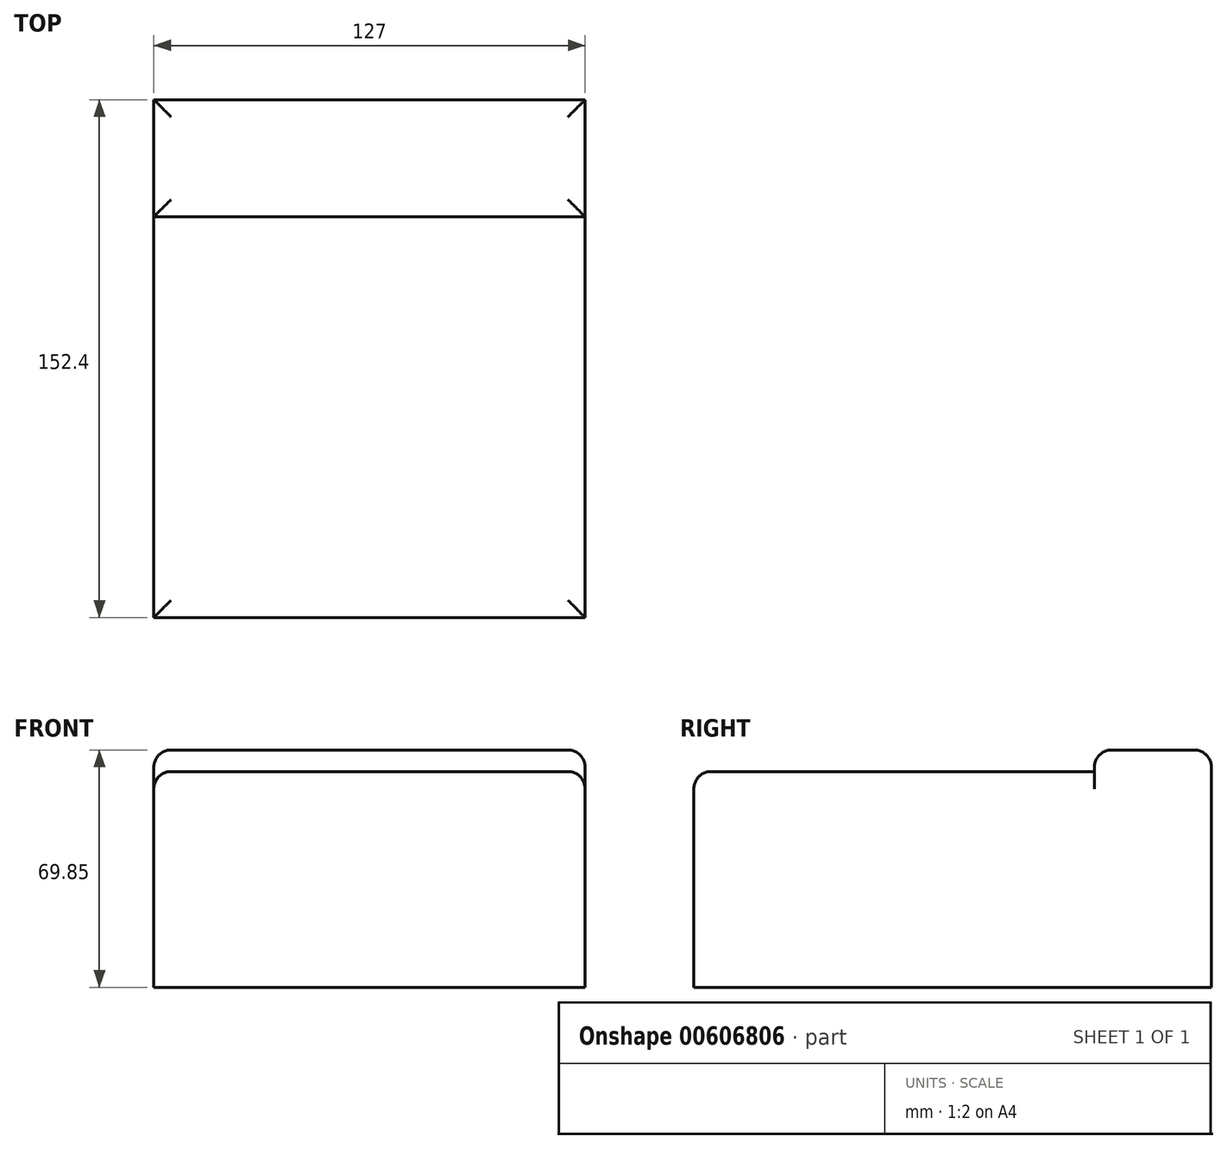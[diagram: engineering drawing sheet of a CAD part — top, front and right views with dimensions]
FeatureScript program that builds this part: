
annotation { "Feature Type Name" : "Feature", "Feature Type Description" : "" }
export const myFeature = defineFeature(function(context is Context, id is Id, definition is map)
    precondition{}
    {
        {
            var Q0;
            Q0=qCreatedBy(makeId("Top.planeOp"),FACE);
            var sketch = newSketch(context, id + "F0", { "sketchPlane" : qUnion([Q0])});
            skLineSegment(sketch, "E0.bottom", {"start": v(-73.34, 101.78) * mm, "end": v(53.66, 101.78) * mm});
            skLineSegment(sketch, "E0.top", {"start": v(-73.34, -50.62) * mm, "end": v(53.66, -50.62) * mm});
            skLineSegment(sketch, "E0.left", {"start": v(-73.34, 101.78) * mm, "end": v(-73.34, -50.62) * mm});
            skLineSegment(sketch, "E0.right", {"start": v(53.66, 101.78) * mm, "end": v(53.66, -50.62) * mm});
            skSolve(sketch);
        }
        {
            var Q0;
            Q0 = qSketchRegion(id + "F0", true);
            extrude(context, id + "F1", {"entities" : qUnion([Q0]), "depth" : 63.5 * mm, "offsetDistance" : 25.4 * mm});
        }
        {
            var Q0;
            Q0=makeQuery(id+"F1.opExtrude","CAP_FACE",FACE,{"disambiguationData":[OSD([sQuery(id+"F0.wireOp",EDGE,"E0.bottom"),sQuery(id+"F0.wireOp",EDGE,"E0.top"),sQuery(id+"F0.wireOp",EDGE,"E0.left"),sQuery(id+"F0.wireOp",EDGE,"E0.right")])],"isStart":false});
            var sketch = newSketch(context, id + "F2", { "sketchPlane" : qUnion([Q0])});
            skLineSegment(sketch, "E1.bottom", {"start": v(-73.34, 101.78) * mm, "end": v(53.66, 101.78) * mm});
            skLineSegment(sketch, "E1.top", {"start": v(-73.34, 67.31) * mm, "end": v(53.66, 67.31) * mm});
            skLineSegment(sketch, "E1.left", {"start": v(-73.34, 101.78) * mm, "end": v(-73.34, 67.31) * mm});
            skLineSegment(sketch, "E1.right", {"start": v(53.66, 101.78) * mm, "end": v(53.66, 67.31) * mm});
            skSolve(sketch);
        }
        {
            var Q0;
            Q0 = qSketchRegion(id + "F2", true);
            extrude(context, id + "F3", {"entities" : qUnion([Q0]), "operationType" : NewBodyOperationType.ADD, "depth" : 6.35 * mm, "offsetDistance" : 25.4 * mm});
        }
        {
            var Q0;
            Q0=makeQuery(id+"F3.opExtrude","CAP_EDGE",EDGE,{"disambiguationData":[OSD([sQuery(id+"F2.wireOp",EDGE,"E1.top")])],"isStart":false});
            var Q1;
            Q1=makeQuery(id+"F1.opExtrude","CAP_EDGE",EDGE,{"disambiguationData":[OSD([sQuery(id+"F0.wireOp",EDGE,"E0.right")])],"isStart":false});
            var Q2;
            Q2=makeQuery(id+"F1.opExtrude","CAP_EDGE",EDGE,{"disambiguationData":[OSD([sQuery(id+"F0.wireOp",EDGE,"E0.top")])],"isStart":false});
            var Q3;
            Q3=makeQuery(id+"F1.opExtrude","CAP_EDGE",EDGE,{"disambiguationData":[OSD([sQuery(id+"F0.wireOp",EDGE,"E0.left")])],"isStart":false});
            var Q4;
            Q4=makeQuery(id+"F3.opExtrude","CAP_EDGE",EDGE,{"disambiguationData":[OSD([sQuery(id+"F2.wireOp",EDGE,"E1.bottom")])],"isStart":false});
            var Q5;
            Q5=makeQuery(id+"F3.opExtrude","CAP_EDGE",EDGE,{"disambiguationData":[OSD([sQuery(id+"F2.wireOp",EDGE,"E1.right")])],"isStart":false});
            var Q6;
            Q6=makeQuery(id+"F3.opExtrude","CAP_EDGE",EDGE,{"disambiguationData":[OSD([sQuery(id+"F2.wireOp",EDGE,"E1.left")])],"isStart":false});
            fillet(context, id + "F4", {"entities" : qUnion([Q0, Q1, Q2, Q3, Q4, Q5, Q6]), "radius" : 5.08 * mm, "tangentPropagation" : true, "allowEdgeOverflow" : false});
        }
    });
